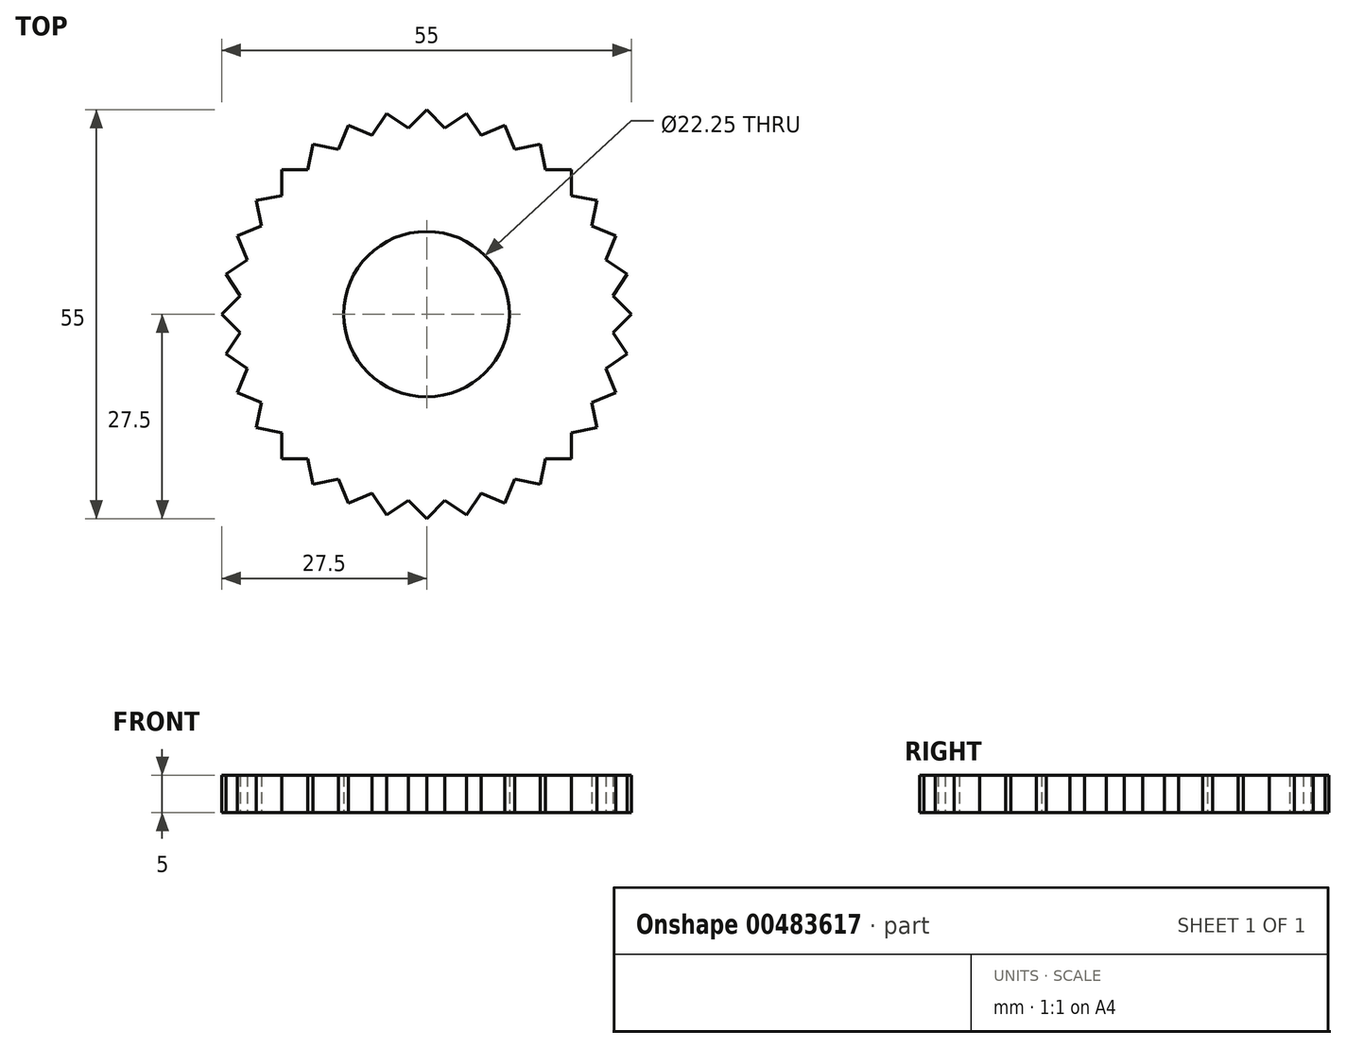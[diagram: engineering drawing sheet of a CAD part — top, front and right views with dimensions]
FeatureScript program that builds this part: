
annotation { "Feature Type Name" : "Feature", "Feature Type Description" : "" }
export const myFeature = defineFeature(function(context is Context, id is Id, definition is map)
    precondition{}
    {
        {
            var Q0;
            Q0=qCreatedBy(makeId("Top.planeOp"),FACE);
            var sketch = newSketch(context, id + "F0", { "sketchPlane" : qUnion([Q0])});
            skCircle(sketch, "E0", {"center": v(0, 0) * mm, "radius": 11.12 * mm});
            skCircle(sketch, "E1", {"center": v(0, 0) * mm, "radius": 27.5 * mm});
            skLineSegment(sketch, "E2", {"start": v(0, 27.5) * mm, "end": v(-2.64, 24.86) * mm});
            skLineSegment(sketch, "E3.MirrorCS", {"start": v(0, 27.5) * mm, "end": v(2.64, 24.86) * mm});
            skLineSegment(sketch, "E4.1.0", {"start": v(-5.36, 26.97) * mm, "end": v(-7.44, 23.87) * mm});
            skLineSegment(sketch, "E4.1.1", {"start": v(-5.36, 26.97) * mm, "end": v(-2.26, 24.9) * mm});
            skLineSegment(sketch, "E4.2.0", {"start": v(-10.52, 25.4) * mm, "end": v(-11.95, 21.96) * mm});
            skLineSegment(sketch, "E4.2.1", {"start": v(-10.52, 25.4) * mm, "end": v(-7.07, 23.98) * mm});
            skLineSegment(sketch, "E4.3.0", {"start": v(-15.28, 22.87) * mm, "end": v(-16, 19.2) * mm});
            skLineSegment(sketch, "E4.3.1", {"start": v(-15.28, 22.87) * mm, "end": v(-11.62, 22.14) * mm});
            skLineSegment(sketch, "E4.4.0", {"start": v(-19.45, 19.45) * mm, "end": v(-19.45, 15.71) * mm});
            skLineSegment(sketch, "E4.4.1", {"start": v(-19.45, 19.45) * mm, "end": v(-15.71, 19.45) * mm});
            skLineSegment(sketch, "E4.5.0", {"start": v(-22.87, 15.28) * mm, "end": v(-22.14, 11.62) * mm});
            skLineSegment(sketch, "E4.5.1", {"start": v(-22.87, 15.28) * mm, "end": v(-19.2, 16) * mm});
            skLineSegment(sketch, "E4.6.0", {"start": v(-25.4, 10.52) * mm, "end": v(-23.98, 7.07) * mm});
            skLineSegment(sketch, "E4.6.1", {"start": v(-25.4, 10.52) * mm, "end": v(-21.96, 11.95) * mm});
            skLineSegment(sketch, "E4.7.0", {"start": v(-26.97, 5.36) * mm, "end": v(-24.9, 2.26) * mm});
            skLineSegment(sketch, "E4.7.1", {"start": v(-26.97, 5.36) * mm, "end": v(-23.87, 7.44) * mm});
            skLineSegment(sketch, "E4.8.0", {"start": v(-27.5, 0) * mm, "end": v(-24.86, -2.64) * mm});
            skLineSegment(sketch, "E4.8.1", {"start": v(-27.5, 0) * mm, "end": v(-24.86, 2.64) * mm});
            skLineSegment(sketch, "E4.9.0", {"start": v(-26.97, -5.36) * mm, "end": v(-23.87, -7.44) * mm});
            skLineSegment(sketch, "E4.9.1", {"start": v(-26.97, -5.36) * mm, "end": v(-24.9, -2.26) * mm});
            skLineSegment(sketch, "E4.10.0", {"start": v(-25.4, -10.52) * mm, "end": v(-21.96, -11.95) * mm});
            skLineSegment(sketch, "E4.10.1", {"start": v(-25.4, -10.52) * mm, "end": v(-23.98, -7.07) * mm});
            skLineSegment(sketch, "E4.11.0", {"start": v(-22.87, -15.28) * mm, "end": v(-19.2, -16) * mm});
            skLineSegment(sketch, "E4.11.1", {"start": v(-22.87, -15.28) * mm, "end": v(-22.14, -11.62) * mm});
            skLineSegment(sketch, "E4.12.0", {"start": v(-19.45, -19.45) * mm, "end": v(-15.71, -19.45) * mm});
            skLineSegment(sketch, "E4.12.1", {"start": v(-19.45, -19.45) * mm, "end": v(-19.45, -15.71) * mm});
            skLineSegment(sketch, "E4.13.0", {"start": v(-15.28, -22.87) * mm, "end": v(-11.62, -22.14) * mm});
            skLineSegment(sketch, "E4.13.1", {"start": v(-15.28, -22.87) * mm, "end": v(-16, -19.2) * mm});
            skLineSegment(sketch, "E4.14.0", {"start": v(-10.52, -25.4) * mm, "end": v(-7.07, -23.98) * mm});
            skLineSegment(sketch, "E4.14.1", {"start": v(-10.52, -25.4) * mm, "end": v(-11.95, -21.96) * mm});
            skLineSegment(sketch, "E4.15.0", {"start": v(-5.36, -26.97) * mm, "end": v(-2.26, -24.9) * mm});
            skLineSegment(sketch, "E4.15.1", {"start": v(-5.36, -26.97) * mm, "end": v(-7.44, -23.87) * mm});
            skLineSegment(sketch, "E4.16.0", {"start": v(0, -27.5) * mm, "end": v(2.64, -24.86) * mm});
            skLineSegment(sketch, "E4.16.1", {"start": v(0, -27.5) * mm, "end": v(-2.64, -24.86) * mm});
            skLineSegment(sketch, "E4.17.0", {"start": v(5.36, -26.97) * mm, "end": v(7.44, -23.87) * mm});
            skLineSegment(sketch, "E4.17.1", {"start": v(5.36, -26.97) * mm, "end": v(2.26, -24.9) * mm});
            skLineSegment(sketch, "E4.18.0", {"start": v(10.52, -25.4) * mm, "end": v(11.95, -21.96) * mm});
            skLineSegment(sketch, "E4.18.1", {"start": v(10.52, -25.4) * mm, "end": v(7.07, -23.98) * mm});
            skLineSegment(sketch, "E4.19.0", {"start": v(15.28, -22.87) * mm, "end": v(16, -19.2) * mm});
            skLineSegment(sketch, "E4.19.1", {"start": v(15.28, -22.87) * mm, "end": v(11.62, -22.14) * mm});
            skLineSegment(sketch, "E4.20.0", {"start": v(19.45, -19.45) * mm, "end": v(19.45, -15.71) * mm});
            skLineSegment(sketch, "E4.20.1", {"start": v(19.45, -19.45) * mm, "end": v(15.71, -19.45) * mm});
            skLineSegment(sketch, "E4.21.0", {"start": v(22.87, -15.28) * mm, "end": v(22.14, -11.62) * mm});
            skLineSegment(sketch, "E4.21.1", {"start": v(22.87, -15.28) * mm, "end": v(19.2, -16) * mm});
            skLineSegment(sketch, "E4.22.0", {"start": v(25.4, -10.52) * mm, "end": v(23.98, -7.07) * mm});
            skLineSegment(sketch, "E4.22.1", {"start": v(25.4, -10.52) * mm, "end": v(21.96, -11.95) * mm});
            skLineSegment(sketch, "E4.23.0", {"start": v(26.97, -5.36) * mm, "end": v(24.9, -2.26) * mm});
            skLineSegment(sketch, "E4.23.1", {"start": v(26.97, -5.36) * mm, "end": v(23.87, -7.44) * mm});
            skLineSegment(sketch, "E4.24.0", {"start": v(27.5, 0) * mm, "end": v(24.86, 2.64) * mm});
            skLineSegment(sketch, "E4.24.1", {"start": v(27.5, 0) * mm, "end": v(24.86, -2.64) * mm});
            skLineSegment(sketch, "E4.25.0", {"start": v(26.97, 5.36) * mm, "end": v(23.87, 7.44) * mm});
            skLineSegment(sketch, "E4.25.1", {"start": v(26.97, 5.36) * mm, "end": v(24.9, 2.26) * mm});
            skLineSegment(sketch, "E4.26.0", {"start": v(25.4, 10.52) * mm, "end": v(21.96, 11.95) * mm});
            skLineSegment(sketch, "E4.26.1", {"start": v(25.4, 10.52) * mm, "end": v(23.98, 7.07) * mm});
            skLineSegment(sketch, "E4.27.0", {"start": v(22.87, 15.28) * mm, "end": v(19.2, 16) * mm});
            skLineSegment(sketch, "E4.27.1", {"start": v(22.87, 15.28) * mm, "end": v(22.14, 11.62) * mm});
            skLineSegment(sketch, "E4.28.0", {"start": v(19.45, 19.45) * mm, "end": v(15.71, 19.45) * mm});
            skLineSegment(sketch, "E4.28.1", {"start": v(19.45, 19.45) * mm, "end": v(19.45, 15.71) * mm});
            skLineSegment(sketch, "E4.29.0", {"start": v(15.28, 22.87) * mm, "end": v(11.62, 22.14) * mm});
            skLineSegment(sketch, "E4.29.1", {"start": v(15.28, 22.87) * mm, "end": v(16, 19.2) * mm});
            skLineSegment(sketch, "E4.30.0", {"start": v(10.52, 25.4) * mm, "end": v(7.07, 23.98) * mm});
            skLineSegment(sketch, "E4.30.1", {"start": v(10.52, 25.4) * mm, "end": v(11.95, 21.96) * mm});
            skLineSegment(sketch, "E4.31.0", {"start": v(5.36, 26.97) * mm, "end": v(2.26, 24.9) * mm});
            skLineSegment(sketch, "E4.31.1", {"start": v(5.36, 26.97) * mm, "end": v(7.44, 23.87) * mm});
            skSolve(sketch);
        }
        {
            var Q0;
            Q0=makeQuery(id+"F0.imprint","IMPRINT",FACE,{"disambiguationData":[TD([[makeQuery(id+"F0.imprint","IMPRINT",EDGE,{"derivedFrom":sQuery(id+"F0.wireOp",EDGE,"E0")}),-1.0]])]});
            extrude(context, id + "F1", {"entities" : qUnion([Q0]), "depth" : 5 * mm});
        }
    });
